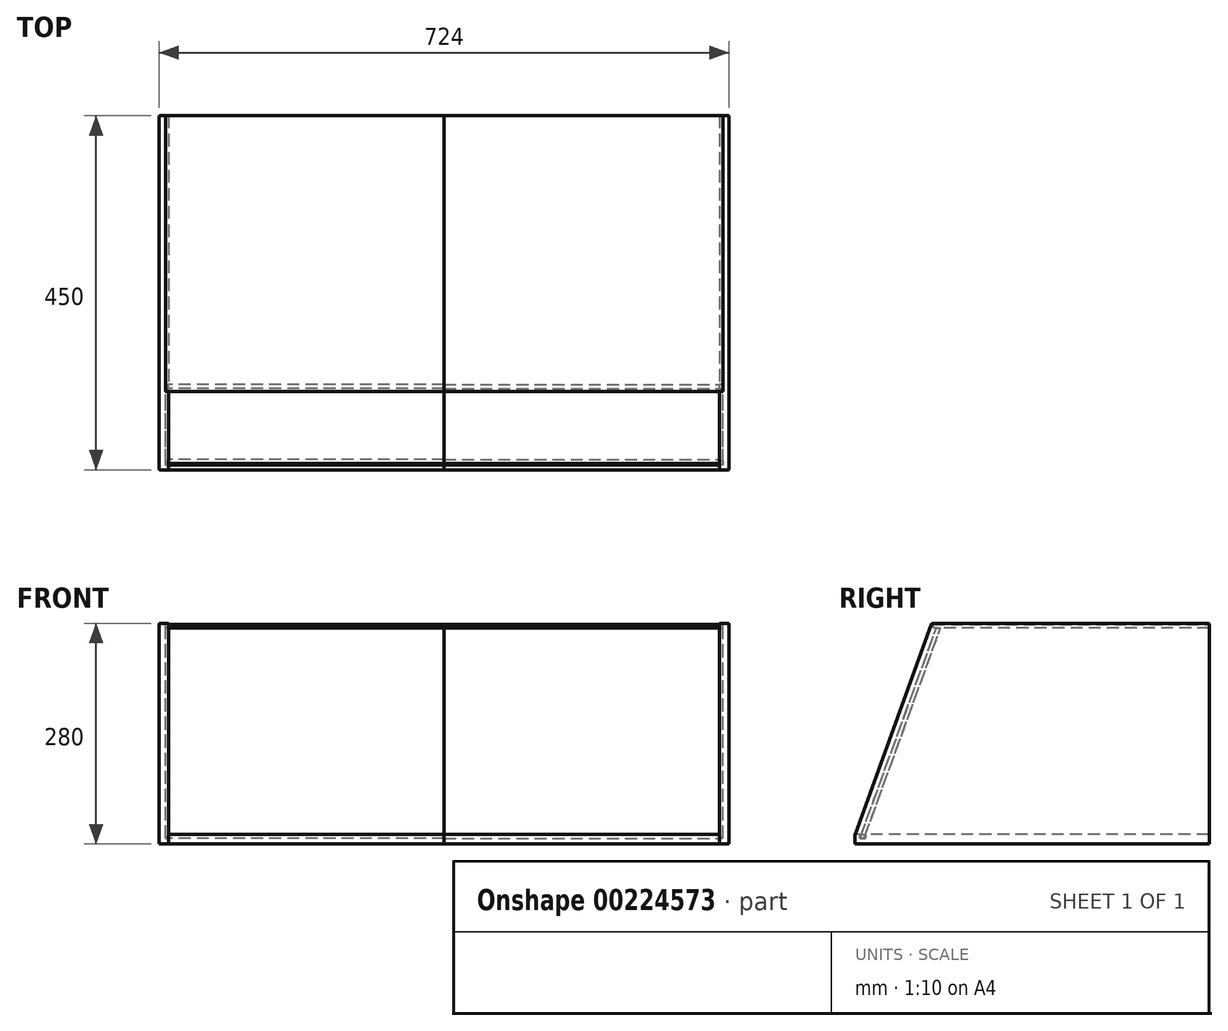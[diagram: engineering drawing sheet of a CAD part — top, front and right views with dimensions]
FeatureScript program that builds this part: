
annotation { "Feature Type Name" : "Feature", "Feature Type Description" : "" }
export const myFeature = defineFeature(function(context is Context, id is Id, definition is map)
    precondition{}
    {
        {
            assignVariable(context, id + "F0", {"name" : "Length", "anyValue" : 700});
        }
        {
            assignVariable(context, id + "F1", {"name" : "ThicknessA", "anyValue" : 12});
        }
        {
            var Q0;
            Q0=qCreatedBy(makeId("Top.planeOp"),FACE);
            var sketch = newSketch(context, id + "F2", { "sketchPlane" : qUnion([Q0])});
            skLineSegment(sketch, "E0.bottom", {"start": v(-350, 450) * mm, "end": v(0, 450) * mm});
            skLineSegment(sketch, "E0.top", {"start": v(-350, 0) * mm, "end": v(0, 0) * mm});
            skLineSegment(sketch, "E0.left", {"start": v(-350, 450) * mm, "end": v(-350, 0) * mm});
            skLineSegment(sketch, "E0.right", {"start": v(0, 450) * mm, "end": v(0, 0) * mm});
            skSolve(sketch);
        }
        {
            var Q0;
            Q0=qSketchRegion(id+"F2",true);
            extrude(context, id + "F3", {"entities" : qUnion([Q0]), "depth" : (getVariable(context, 'ThicknessA')) * mm});
        }
        {
            var Q0;
            Q0=makeQuery(id+"F3.opExtrude","SWEPT_FACE",FACE,{"disambiguationData":[OSD([sQuery(id+"F2.wireOp",EDGE,"E0.left")])]});
            var sketch = newSketch(context, id + "F4", { "sketchPlane" : qUnion([Q0])});
            skLineSegment(sketch, "E1.0", {"start": v(-450, 0) * mm, "end": v(0, 0) * mm});
            skLineSegment(sketch, "E2", {"start": v(-450, 0) * mm, "end": v(-450, 280) * mm});
            skLineSegment(sketch, "E3", {"start": v(0, 0) * mm, "end": v(0, 12) * mm});
            skLineSegment(sketch, "E4", {"start": v(-450, 280) * mm, "end": v(-97.54, 280) * mm});
            skLineSegment(sketch, "E5", {"start": v(0, 12) * mm, "end": v(-97.54, 280) * mm});
            skLineSegment(sketch, "E6", {"start": v(0, 12) * mm, "end": v(-450, 12) * mm, "construction": true});
            skLineSegment(sketch, "E7", {"start": v(-6.16, 7) * mm, "end": v(-105.53, 280) * mm});
            skLineSegment(sketch, "E8", {"start": v(-11.48, 7) * mm, "end": v(-110.85, 280) * mm});
            skLineSegment(sketch, "E9", {"start": v(-2.4, 7) * mm, "end": v(-45.45, 7) * mm, "construction": true});
            skLineSegment(sketch, "E10", {"start": v(-6.16, 7) * mm, "end": v(-11.48, 7) * mm});
            skLineSegment(sketch, "E11", {"start": v(-450, 274) * mm, "end": v(-99.34, 274) * mm});
            skLineSegment(sketch, "E12", {"start": v(-99.34, 274) * mm, "end": v(-99.34, 280) * mm});
            skPoint(sketch, "E13", {"position": v(-103.34, 274) * mm});
            skLineSegment(sketch, "E14", {"start": v(-6.16, 7) * mm, "end": v(-6.16, 12) * mm, "construction": true});
            skLineSegment(sketch, "E15", {"start": v(-13.3, 12) * mm, "end": v(-13.3, 7) * mm, "construction": true});
            skSolve(sketch);
        }
        {
            var Q0;
            {var subQ2=sQuery(id+"F4.wireOp",EDGE,"E1.0");Q0=makeQuery(id+"F4.imprint","IMPRINT",FACE,{"disambiguationData":[TD([[makeQuery(id+"F4.imprint","IMPRINT",EDGE,{"derivedFrom":subQ2}),1.0]])]});}
            var Q1;
            {var subQ0=sQuery(id+"F4.wireOp",EDGE,"E10");Q1=makeQuery(id+"F4.imprint","IMPRINT",FACE,{"disambiguationData":[TD([[makeQuery(id+"F4.imprint","IMPRINT",EDGE,{"derivedFrom":subQ0}),-1.0]])]});}
            var Q2;
            {var subQ5=sQuery(id+"F4.wireOp",EDGE,"E5");Q2=makeQuery(id+"F4.imprint","IMPRINT",FACE,{"disambiguationData":[TD([[makeQuery(id+"F4.imprint","IMPRINT",EDGE,{"derivedFrom":subQ5}),1.0]])]});}
            var Q3;
            {var subQ0=sQuery(id+"F4.wireOp",EDGE,"E11");var subQ1=sQuery(id+"F4.wireOp",EDGE,"E7");var subQ2=makeQuery(id+"F4.imprint","INTERSECT",VERTEX,{"derivedFrom":[subQ1,subQ0]});Q3=makeQuery(id+"F4.imprint","IMPRINT",FACE,{"disambiguationData":[TD([[makeQuery(id+"F4.imprint","IMPRINT",EDGE,{"disambiguationData":[TD([[subQ2,1.0]])],"derivedFrom":subQ1}),1.0]])]});}
            var Q4;
            {var subQ0=sQuery(id+"F4.wireOp",EDGE,"E2");var subQ3=sQuery(id+"F4.wireOp",EDGE,"E11");var subQ4=makeQuery(id+"F4.imprint","INTERSECT",VERTEX,{"derivedFrom":[subQ0,subQ3]});Q4=makeQuery(id+"F4.imprint","IMPRINT",FACE,{"disambiguationData":[TD([[makeQuery(id+"F4.imprint","IMPRINT",EDGE,{"disambiguationData":[TD([[subQ4,1.0]])],"derivedFrom":subQ0}),-1.0]])]});}
            var Q5;
            {var subQ3=sQuery(id+"F4.wireOp",EDGE,"E12");Q5=makeQuery(id+"F4.imprint","IMPRINT",FACE,{"disambiguationData":[TD([[makeQuery(id+"F4.imprint","IMPRINT",EDGE,{"derivedFrom":subQ3}),1.0]])]});}
            var Q6;
            {var subQ0=sQuery(id+"F4.wireOp",EDGE,"E7");var subQ1=sQuery(id+"F4.wireOp",EDGE,"E4");var subQ2=makeQuery(id+"F4.imprint","INTERSECT",VERTEX,{"derivedFrom":[subQ1,subQ0]});Q6=makeQuery(id+"F4.imprint","IMPRINT",FACE,{"disambiguationData":[TD([[makeQuery(id+"F4.imprint","IMPRINT",EDGE,{"disambiguationData":[TD([[subQ2,1.0]])],"derivedFrom":subQ1}),-1.0]])]});}
            var Q7;
            {var subQ0=sQuery(id+"F4.wireOp",EDGE,"E4");var subQ1=sQuery(id+"F4.wireOp",EDGE,"E2");var subQ2=makeQuery(id+"F4.imprint","INTERSECT",VERTEX,{"derivedFrom":[subQ1,subQ0]});Q7=makeQuery(id+"F4.imprint","IMPRINT",FACE,{"disambiguationData":[TD([[makeQuery(id+"F4.imprint","IMPRINT",EDGE,{"disambiguationData":[TD([[subQ2,1.0]])],"derivedFrom":subQ1}),-1.0]])]});}
            extrude(context, id + "F5", {"entities" : qUnion([Q0, Q1, Q2, Q3, Q4, Q5, Q6, Q7]), "depth" : (getVariable(context, 'ThicknessA')) * mm, "offsetDistance" : 25 * mm});
        }
        {
            var Q0;
            {var subQ0=sQuery(id+"F4.wireOp",EDGE,"E10");Q0=makeQuery(id+"F4.imprint","IMPRINT",FACE,{"disambiguationData":[TD([[makeQuery(id+"F4.imprint","IMPRINT",EDGE,{"derivedFrom":subQ0}),-1.0]])]});}
            var Q1;
            {var subQ0=sQuery(id+"F4.wireOp",EDGE,"E11");var subQ1=sQuery(id+"F4.wireOp",EDGE,"E7");var subQ2=makeQuery(id+"F4.imprint","INTERSECT",VERTEX,{"derivedFrom":[subQ1,subQ0]});Q1=makeQuery(id+"F4.imprint","IMPRINT",FACE,{"disambiguationData":[TD([[makeQuery(id+"F4.imprint","IMPRINT",EDGE,{"disambiguationData":[TD([[subQ2,1.0]])],"derivedFrom":subQ1}),1.0]])]});}
            var Q2;
            {var subQ3=sQuery(id+"F4.wireOp",EDGE,"E12");Q2=makeQuery(id+"F4.imprint","IMPRINT",FACE,{"disambiguationData":[TD([[makeQuery(id+"F4.imprint","IMPRINT",EDGE,{"derivedFrom":subQ3}),1.0]])]});}
            var Q3;
            {var subQ0=sQuery(id+"F4.wireOp",EDGE,"E7");var subQ1=sQuery(id+"F4.wireOp",EDGE,"E4");var subQ2=makeQuery(id+"F4.imprint","INTERSECT",VERTEX,{"derivedFrom":[subQ1,subQ0]});Q3=makeQuery(id+"F4.imprint","IMPRINT",FACE,{"disambiguationData":[TD([[makeQuery(id+"F4.imprint","IMPRINT",EDGE,{"disambiguationData":[TD([[subQ2,1.0]])],"derivedFrom":subQ1}),-1.0]])]});}
            var Q4;
            {var subQ0=sQuery(id+"F4.wireOp",EDGE,"E4");var subQ1=sQuery(id+"F4.wireOp",EDGE,"E2");var subQ2=makeQuery(id+"F4.imprint","INTERSECT",VERTEX,{"derivedFrom":[subQ1,subQ0]});Q4=makeQuery(id+"F4.imprint","IMPRINT",FACE,{"disambiguationData":[TD([[makeQuery(id+"F4.imprint","IMPRINT",EDGE,{"disambiguationData":[TD([[subQ2,1.0]])],"derivedFrom":subQ1}),-1.0]])]});}
            extrude(context, id + "F6", {"entities" : qUnion([Q0, Q1, Q2, Q3, Q4]), "operationType" : NewBodyOperationType.REMOVE, "depth" : (getVariable(context, 'ThicknessA') * 1 / 3) * mm, "offsetDistance" : 25 * mm});
        }
        {
            var Q0;
            Q0=makeQuery(id+"F6.boolean.opBoolean","COPY",FACE,{"derivedFrom":makeQuery(id+"F6.opExtrude","CAP_FACE",FACE,{"disambiguationData":[OSD([sQuery(id+"F4.wireOp",EDGE,"E2"),sQuery(id+"F4.wireOp",EDGE,"E4"),sQuery(id+"F4.wireOp",EDGE,"E7"),sQuery(id+"F4.wireOp",EDGE,"E8"),sQuery(id+"F4.wireOp",EDGE,"E10"),sQuery(id+"F4.wireOp",EDGE,"E11"),sQuery(id+"F4.wireOp",EDGE,"E12")])],"isStart":false})});
            var sketch = newSketch(context, id + "F7", { "sketchPlane" : qUnion([Q0])});
            skLineSegment(sketch, "E16.0", {"start": v(6.78, 8.71) * mm, "end": v(103.34, 274) * mm});
            skLineSegment(sketch, "E17.0", {"start": v(11.48, 7) * mm, "end": v(108.66, 274) * mm});
            skLineSegment(sketch, "E18", {"start": v(103.34, 274) * mm, "end": v(108.66, 274) * mm});
            skLineSegment(sketch, "E19", {"start": v(11.48, 7) * mm, "end": v(6.78, 8.71) * mm});
            skPoint(sketch, "E20.orphan", {"position": v(6.16, 7) * mm});
            skLineSegment(sketch, "E21.0", {"start": v(450, 274) * mm, "end": v(99.34, 274) * mm});
            skLineSegment(sketch, "E22", {"start": v(99.34, 274) * mm, "end": v(99.34, 279) * mm});
            skLineSegment(sketch, "E23", {"start": v(99.34, 279) * mm, "end": v(450, 279) * mm});
            skLineSegment(sketch, "E24", {"start": v(450, 279) * mm, "end": v(450, 274) * mm});
            skSolve(sketch);
        }
        {
            var Q0;
            {var subQ0=sQuery(id+"F7.wireOp",EDGE,"E16.0");Q0=makeQuery(id+"F7.imprint","IMPRINT",FACE,{"disambiguationData":[TD([[makeQuery(id+"F7.imprint","IMPRINT",EDGE,{"derivedFrom":subQ0}),-1.0]])]});}
            extrude(context, id + "F8", {"entities" : qUnion([Q0]), "depth" : (getVariable(context, 'Length') / 2 + getVariable(context, 'ThicknessA') * 1 / 3) * mm, "offsetDistance" : 25 * mm});
        }
        {
            var Q0;
            {var subQ0=sQuery(id+"F7.wireOp",EDGE,"E22");Q0=makeQuery(id+"F7.imprint","IMPRINT",FACE,{"disambiguationData":[TD([[makeQuery(id+"F7.imprint","IMPRINT",EDGE,{"derivedFrom":subQ0}),-1.0]])]});}
            extrude(context, id + "F9", {"entities" : qUnion([Q0]), "depth" : (getVariable(context, 'Length') / 2 + getVariable(context, 'ThicknessA') * 1 / 3) * mm, "offsetDistance" : 25 * mm});
        }
        {
            var Q0;
            {var subQ2=sQuery(id+"F4.wireOp",EDGE,"E1.0");Q0=makeQuery(id+"F4.imprint","IMPRINT",FACE,{"disambiguationData":[TD([[makeQuery(id+"F4.imprint","IMPRINT",EDGE,{"derivedFrom":subQ2}),1.0]])]});}
            var sketch = newSketch(context, id + "F10", { "sketchPlane" : qUnion([Q0])});
            skLineSegment(sketch, "E25.0", {"start": v(-13.3, 12) * mm, "end": v(-13.3, 7) * mm});
            skLineSegment(sketch, "E26.0", {"start": v(-6.16, 7) * mm, "end": v(-6.16, 12) * mm});
            skLineSegment(sketch, "E27", {"start": v(-13.3, 12) * mm, "end": v(-6.16, 12) * mm});
            skLineSegment(sketch, "E28", {"start": v(-6.16, 7) * mm, "end": v(-13.3, 7) * mm});
            skSolve(sketch);
        }
        {
            var Q0;
            Q0 = qSketchRegion(id + "F10", true);
            extrude(context, id + "F11", {"entities" : qUnion([Q0]), "operationType" : NewBodyOperationType.REMOVE, "endBound" : BoundingType.THROUGH_ALL, "oppositeDirection" : true, "depth" : 25 * mm, "offsetDistance" : 25 * mm});
        }
        {
            var Q0;
            Q0=makeQuery(id+"F5.opExtrude","CAP_EDGE",EDGE,{"disambiguationData":[OSD([sQuery(id+"F4.wireOp",EDGE,"E5")])],"isStart":false});
            var Q1;
            Q1=makeQuery(id+"F5.opExtrude","CAP_EDGE",EDGE,{"disambiguationData":[OSD([sQuery(id+"F4.wireOp",EDGE,"E4")])],"isStart":false});
            var Q2;
            Q2=makeQuery(id+"F5.opExtrude","SWEPT_EDGE",EDGE,{"disambiguationData":[OSD([sQuery(id+"F4.wireOp",EDGE,"E4"),sQuery(id+"F4.wireOp",EDGE,"E5")])]});
            var Q3;
            Q3=makeQuery(id+"F5.opExtrude","CAP_EDGE",EDGE,{"disambiguationData":[OSD([sQuery(id+"F4.wireOp",EDGE,"E2")])],"isStart":false});
            var Q4;
            Q4=makeQuery(id+"F3.opExtrude","CAP_EDGE",EDGE,{"disambiguationData":[OSD([sQuery(id+"F2.wireOp",EDGE,"E0.top")])],"isStart":false});
            var Q5;
            Q5=makeQuery(id+"F3.opExtrude","CAP_EDGE",EDGE,{"disambiguationData":[OSD([sQuery(id+"F2.wireOp",EDGE,"E0.bottom")])],"isStart":false});
            var Q6;
            Q6=makeQuery(id+"F5.opExtrude","CAP_EDGE",EDGE,{"disambiguationData":[OSD([sQuery(id+"F4.wireOp",EDGE,"E3")])],"isStart":false});
            var Q7;
            Q7=makeQuery(id+"F5.opExtrude","SWEPT_EDGE",EDGE,{"disambiguationData":[OSD([sQuery(id+"F4.wireOp",EDGE,"E2"),sQuery(id+"F4.wireOp",EDGE,"E4")])]});
            fillet(context, id + "F12", {"entities" : qUnion([Q0, Q1, Q2, Q3, Q4, Q5, Q6, Q7]), "radius" : 1 * mm, "tangentPropagation" : true, "allowEdgeOverflow" : false});
        }
        {
            var Q0;
            Q0=makeQuery(id+"F5.opExtrude","SWEPT_EDGE",EDGE,{"disambiguationData":[OSD([sQuery(id+"F2.wireOp",EDGE,"E0.left"),sQuery(id+"F4.wireOp",EDGE,"E3"),sQuery(id+"F4.wireOp",EDGE,"E5")])]});
            fillet(context, id + "F13", {"entities" : qUnion([Q0]), "radius" : 5 * mm, "tangentPropagation" : true, "allowEdgeOverflow" : false});
        }
        {
            var Q0;
            Q0=makeQuery(id+"F5.opExtrude","SWEPT_BODY",BODY,{"disambiguationData":[OSD([sQuery(id+"F4.wireOp",EDGE,"E1.0"),sQuery(id+"F4.wireOp",EDGE,"E2"),sQuery(id+"F4.wireOp",EDGE,"E3"),sQuery(id+"F4.wireOp",EDGE,"E4"),sQuery(id+"F4.wireOp",EDGE,"E5")])]});
            var Q1;
            Q1=makeQuery(id+"F9.opExtrude","SWEPT_BODY",BODY,{"disambiguationData":[OSD([sQuery(id+"F7.wireOp",EDGE,"E21.0"),sQuery(id+"F7.wireOp",EDGE,"E22"),sQuery(id+"F7.wireOp",EDGE,"E23"),sQuery(id+"F7.wireOp",EDGE,"E24")])]});
            var Q2;
            Q2=makeQuery(id+"F3.opExtrude","SWEPT_BODY",BODY,{"disambiguationData":[OSD([sQuery(id+"F2.wireOp",EDGE,"E0.bottom"),sQuery(id+"F2.wireOp",EDGE,"E0.top"),sQuery(id+"F2.wireOp",EDGE,"E0.left"),sQuery(id+"F2.wireOp",EDGE,"E0.right")])]});
            var Q3;
            Q3=makeQuery(id+"F8.opExtrude","SWEPT_BODY",BODY,{"disambiguationData":[OSD([sQuery(id+"F7.wireOp",EDGE,"E16.0"),sQuery(id+"F7.wireOp",EDGE,"E17.0"),sQuery(id+"F7.wireOp",EDGE,"E19"),sQuery(id+"F7.wireOp",EDGE,"E21.0")])]});
            var Q4;
            Q4=makeQuery(id+"F3.opExtrude","SWEPT_FACE",FACE,{"disambiguationData":[OSD([sQuery(id+"F2.wireOp",EDGE,"E0.right")])]});
            mirror(context, id + "F14", {"entities" : qUnion([Q0, Q1, Q2, Q3]), "mirrorPlane" : qUnion([Q4])});
        }
    });
